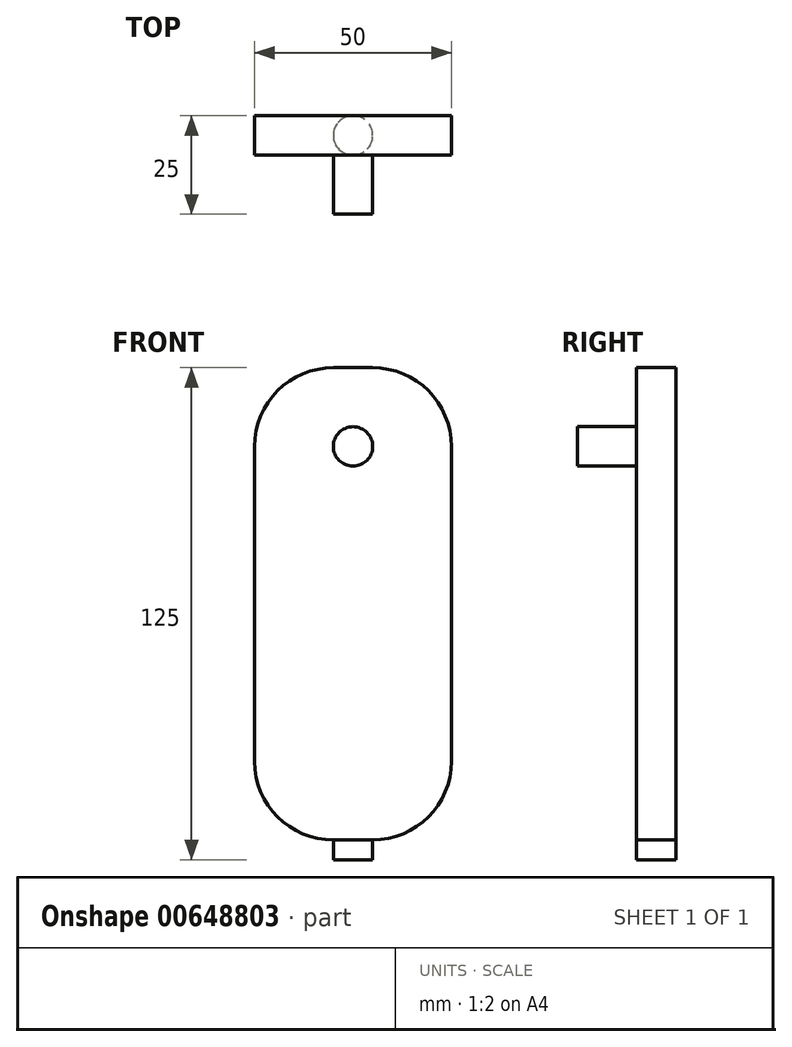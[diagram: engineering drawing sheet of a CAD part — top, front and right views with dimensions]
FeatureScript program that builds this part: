
annotation { "Feature Type Name" : "Feature", "Feature Type Description" : "" }
export const myFeature = defineFeature(function(context is Context, id is Id, definition is map)
    precondition{}
    {
        {
            var Q0;
            Q0=qCreatedBy(makeId("Top.planeOp"),FACE);
            var sketch = newSketch(context, id + "F0", { "sketchPlane" : qUnion([Q0])});
            skLineSegment(sketch, "E0.bottom", {"start": v(25, -5) * mm, "end": v(-25, -5) * mm});
            skLineSegment(sketch, "E0.top", {"start": v(25, 5) * mm, "end": v(-25, 5) * mm});
            skLineSegment(sketch, "E0.left", {"start": v(25, -5) * mm, "end": v(25, 5) * mm});
            skLineSegment(sketch, "E0.right", {"start": v(-25, -5) * mm, "end": v(-25, 5) * mm});
            skPoint(sketch, "E0.middle", {"position": v(0, 0) * mm});
            skSolve(sketch);
        }
        {
            var Q0;
            Q0=makeQuery(id+"F0.imprint","IMPRINT",FACE,{"disambiguationData":[TD([[makeQuery(id+"F0.imprint","IMPRINT",EDGE,{"derivedFrom":sQuery(id+"F0.wireOp",EDGE,"E0.bottom")}),-1.0]])]});
            extrude(context, id + "F1", {"entities" : qUnion([Q0]), "depth" : 120 * mm, "offsetDistance" : 25 * mm});
        }
        {
            var Q0;
            Q0=makeQuery(id+"F1.opExtrude","SWEPT_FACE",FACE,{"disambiguationData":[OSD([sQuery(id+"F0.wireOp",EDGE,"E0.bottom")])]});
            var sketch = newSketch(context, id + "F2", { "sketchPlane" : qUnion([Q0])});
            skCircle(sketch, "E1", {"center": v(0, 100) * mm, "radius": 5 * mm});
            skSolve(sketch);
        }
        {
            var Q0;
            Q0=makeQuery(id+"F2.imprint","IMPRINT",FACE,{"disambiguationData":[TD([[makeQuery(id+"F2.imprint","IMPRINT",EDGE,{"derivedFrom":sQuery(id+"F2.wireOp",EDGE,"E1")}),1.0]])]});
            extrude(context, id + "F3", {"entities" : qUnion([Q0]), "operationType" : NewBodyOperationType.ADD, "depth" : 15 * mm, "offsetDistance" : 25 * mm});
        }
        {
            var Q0;
            Q0=makeQuery(id+"F1.opExtrude","CAP_FACE",FACE,{"disambiguationData":[OSD([sQuery(id+"F0.wireOp",EDGE,"E0.bottom"),sQuery(id+"F0.wireOp",EDGE,"E0.top"),sQuery(id+"F0.wireOp",EDGE,"E0.left"),sQuery(id+"F0.wireOp",EDGE,"E0.right")])],"isStart":true});
            var sketch = newSketch(context, id + "F4", { "sketchPlane" : qUnion([Q0])});
            skCircle(sketch, "E2", {"center": v(0, 0) * mm, "radius": 5 * mm});
            skSolve(sketch);
        }
        {
            var Q0;
            {var subQ0=sQuery(id+"F4.wireOp",EDGE,"E2");var subQ1=makeQuery(id+"F4.imprint","INTERSECT",VERTEX,{"derivedFrom":[makeQuery(id+"F1.opExtrude","CAP_EDGE",EDGE,{"disambiguationData":[OSD([sQuery(id+"F0.wireOp",EDGE,"E0.bottom")])],"isStart":true}),subQ0]});Q0=makeQuery(id+"F4.imprint","IMPRINT",FACE,{"disambiguationData":[TD([[makeQuery(id+"F4.imprint","IMPRINT",EDGE,{"disambiguationData":[TD([[subQ1,-1.0]])],"derivedFrom":subQ0}),1.0]])]});}
            extrude(context, id + "F5", {"entities" : qUnion([Q0]), "operationType" : NewBodyOperationType.ADD, "depth" : 5 * mm, "offsetDistance" : 25 * mm});
        }
        {
            var Q0;
            Q0=makeQuery(id+"F1.opExtrude","CAP_EDGE",EDGE,{"disambiguationData":[OSD([sQuery(id+"F0.wireOp",EDGE,"E0.left")])],"isStart":true});
            var Q1;
            Q1=makeQuery(id+"F1.opExtrude","CAP_EDGE",EDGE,{"disambiguationData":[OSD([sQuery(id+"F0.wireOp",EDGE,"E0.right")])],"isStart":true});
            var Q2;
            Q2=makeQuery(id+"F1.opExtrude","CAP_EDGE",EDGE,{"disambiguationData":[OSD([sQuery(id+"F0.wireOp",EDGE,"E0.right")])],"isStart":false});
            var Q3;
            Q3=makeQuery(id+"F1.opExtrude","CAP_EDGE",EDGE,{"disambiguationData":[OSD([sQuery(id+"F0.wireOp",EDGE,"E0.left")])],"isStart":false});
            fillet(context, id + "F6", {"entities" : qUnion([Q0, Q1, Q2, Q3]), "radius" : 20 * mm, "tangentPropagation" : true, "allowEdgeOverflow" : false});
        }
    });
